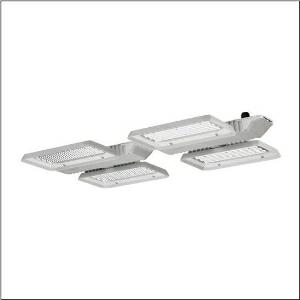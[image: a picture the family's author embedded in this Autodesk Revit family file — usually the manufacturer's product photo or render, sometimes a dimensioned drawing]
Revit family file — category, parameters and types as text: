
# Revit family: highbay_11_51hlasd24mga
name_source: partatom
category: Lighting Fixtures
units: mm (PartAtom-declared; Revit-internal decimal feet)

## family parameters
Cut with Voids When Loaded = No
Host = Face
Light Source = No
Part Type = Normal
Room Calculation Point = No
Round Connector Dimension = Use Diameter
Shared = No

## types (1)
- --- (1 x LED, 28800 lm, 162.6 W, 4000K)
    Apparent Load = 163 VA
    CIE Flux Codes = 89 96 99 100 100
    Color Rendering = 80
    Color Temperature = 4000K
    Default Elevation = 1800 mm
    Description = Highbay 11, LED high bay luminaire, primary light control with lens, of PMMA, light emission: direct distribution, primary light characteristic: symmetric, installation type: suspended mounting, for 2x 2 x LED rated luminous flux: 28.800 lm, light colour: 840, colour temperature: 4000K, control gear: ECG DALI, with terminal, 5-pole, max. 2.5mm², mains connection: 230..240V, AC, 50/60Hz, rated input power: 163W, LED unit, of diecast aluminium, unplated, bead blasted, silver, length: 940 mm, width: 500 mm, height: 65mm, housing, of diecast aluminium, uncoated, bead blasted, silver, protection rating (complete): IP20, insulation class (complete): insulation class I (protective earthing), certification: CE, ENEC, VDE, protection symbol: D, ball protection: ball impact resistant according to DIN VDE 0710 part 13 (with chain suspension), permissible ambient temperature for indoor applications: -35..+55°C, corresponds to IFS (International Featured Standards) requirements for safety and quality in the food industry, reducing of maximum allowable ambient temperature of 5°C with ceiling mounting, packaging unit: 1 piece
    Height = 95 mm
    Lamp = 1 x LED
    Lamp Light Flux = 28800 lm
    Lamp Power = 162.6 W
    Lamp count = 1
    Length = 939 mm
    Luminous efficacy = 177 lm/W
    Manufacturer = Siteco
    ModVariant = No
    Model = 51HLASD24MGA
    Mounting Place = Ceiling
    Mounting Type = Pendant
    Number of Poles = 1
    OnlyDefault = Yes
    Power Factor = 1
    Product Name = Highbay 11
    Product group = LED high bay luminaire
    ProductGroupID = 903
    Protection Class = Protection class I
    Protection Degree = IP 20
    RLX_Detail_Level = 1
    RlxData = <blob elided: 64849 chars, md5=58e75823>
    Socket = socket
    Standby Power = 0 W
    System Light Flux = 28800 lm
    System Power = 163 W
    Type Comments = factory setting: luminous flux: 100 % | dim-lin: 254 | 460 mA
    Type Image = l_1006021.jpg
    URL = http://relux.com
    VarID = @adj_137441
    Voltage = 0 V
    Weight = 0.00 kg
    Width = 501 mm

## geometry (parser evidence)
native form markers: Blend x4, Sweep x13
no freeform markers — native parametric forms only
